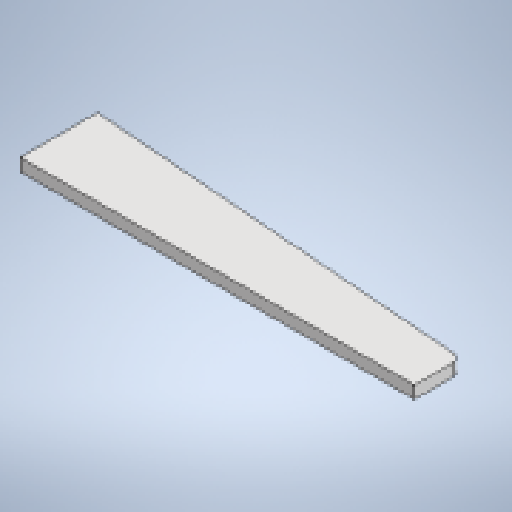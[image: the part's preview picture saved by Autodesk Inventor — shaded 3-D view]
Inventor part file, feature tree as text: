
AUTODESK INVENTOR PART (.ipt)
format: ipt  version: 2025.1 (Build 291241020, 241B)  size: 276,992 bytes
history: native  units: mm
features: other x2, sheet_metal_op x1, chamfer x1, sketch x1
ambient origin geometry x8: Origin, YZ Plane, XZ Plane, XY Plane, X Axis, Y Axis, Z Axis, Center Point
bodies: Body1 (feature_tree)
feature tree (5):
  sheet_metal_op  "Face1"
  chamfer  "Corner Round1"
  sketch  "Sketch3"  dims[d11=300.0mm d12=30.0mm d13=45.0mm d14=50.0mm d15=8.0mm d16=6.0mm]
  other  "Plate1"
  other  "Definition1"
